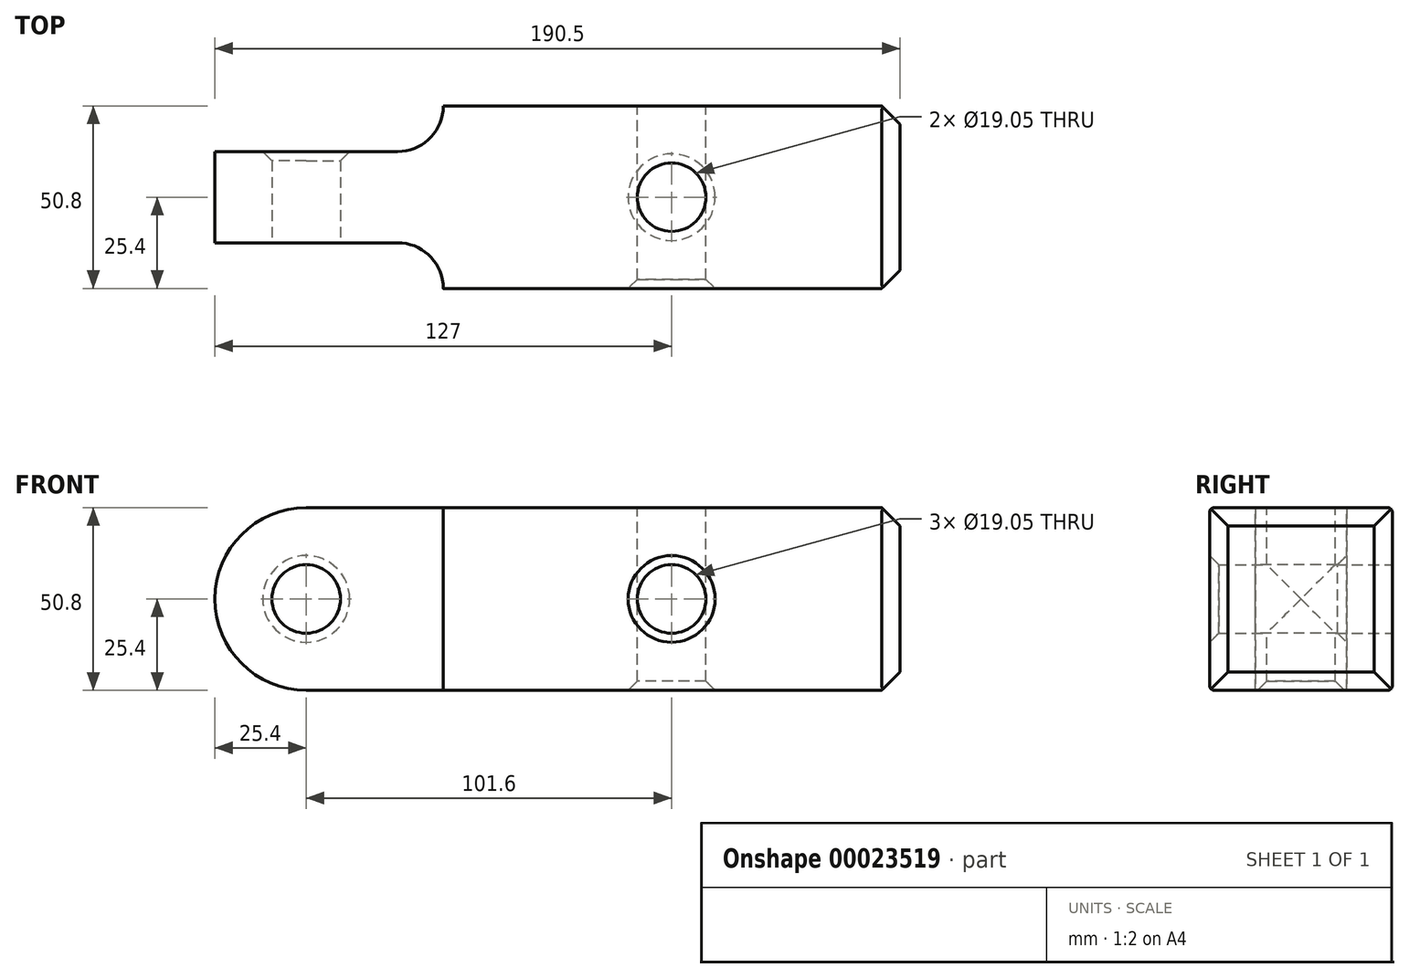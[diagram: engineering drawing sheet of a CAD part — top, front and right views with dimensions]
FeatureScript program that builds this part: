
annotation { "Feature Type Name" : "Feature", "Feature Type Description" : "" }
export const myFeature = defineFeature(function(context is Context, id is Id, definition is map)
    precondition{}
    {
        {
            var Q0;
            Q0=qCreatedBy(makeId("Right.planeOp"),FACE);
            var sketch = newSketch(context, id + "F0", { "sketchPlane" : qUnion([Q0])});
            skLineSegment(sketch, "E0.bottom", {"start": v(0, 0) * mm, "end": v(50.8, 0) * mm});
            skLineSegment(sketch, "E0.top", {"start": v(0, 50.8) * mm, "end": v(50.8, 50.8) * mm});
            skLineSegment(sketch, "E0.left", {"start": v(0, 0) * mm, "end": v(0, 50.8) * mm});
            skLineSegment(sketch, "E0.right", {"start": v(50.8, 0) * mm, "end": v(50.8, 50.8) * mm});
            skSolve(sketch);
        }
        {
            var Q0;
            Q0 = qSketchRegion(id + "F0", true);
            extrude(context, id + "F1", {"entities" : qUnion([Q0]), "depth" : 190.5 * mm});
        }
        {
            var Q0;
            Q0=makeQuery(id+"F1.opExtrude","CAP_FACE",FACE,{"disambiguationData":[OSD([sQuery(id+"F0.wireOp",EDGE,"E0.bottom"),sQuery(id+"F0.wireOp",EDGE,"E0.top"),sQuery(id+"F0.wireOp",EDGE,"E0.left"),sQuery(id+"F0.wireOp",EDGE,"E0.right")])],"isStart":false});
            chamfer(context, id + "F2", {"entities" : qUnion([Q0]), "width" : 5.08 * mm, "tangentPropagation" : true});
        }
        {
            var Q0;
            Q0=makeQuery(id+"F1.opExtrude","SWEPT_FACE",FACE,{"disambiguationData":[OSD([sQuery(id+"F0.wireOp",EDGE,"E0.right")])]});
            var sketch = newSketch(context, id + "F3", { "sketchPlane" : qUnion([Q0])});
            skCircle(sketch, "E1", {"center": v(-127, 25.4) * mm, "radius": 9.53 * mm});
            skLineSegment(sketch, "E2", {"start": v(0, 25.4) * mm, "end": v(-185.42, 25.4) * mm, "construction": true});
            skSolve(sketch);
        }
        {
            var Q0;
            Q0 = qSketchRegion(id + "F3", true);
            extrude(context, id + "F4", {"entities" : qUnion([Q0]), "operationType" : NewBodyOperationType.REMOVE, "endBound" : BoundingType.THROUGH_ALL, "oppositeDirection" : true, "depth" : 25.4 * mm});
        }
        {
            var Q0;
            Q0=makeQuery(id+"F1.opExtrude","SWEPT_EDGE",EDGE,{"disambiguationData":[OSD([sQuery(id+"F0.wireOp",EDGE,"E0.top"),sQuery(id+"F0.wireOp",EDGE,"E0.right")])]});
            var Q1;
            Q1=makeQuery(id+"F1.opExtrude","SWEPT_EDGE",EDGE,{"disambiguationData":[OSD([sQuery(id+"F0.wireOp",EDGE,"E0.top"),sQuery(id+"F0.wireOp",EDGE,"E0.left")])]});
            var Q2;
            Q2=makeQuery(id+"F1.opExtrude","SWEPT_EDGE",EDGE,{"disambiguationData":[OSD([sQuery(id+"F0.wireOp",EDGE,"E0.bottom"),sQuery(id+"F0.wireOp",EDGE,"E0.right")])]});
            var Q3;
            Q3=makeQuery(id+"F1.opExtrude","SWEPT_EDGE",EDGE,{"disambiguationData":[OSD([sQuery(id+"F0.wireOp",EDGE,"E0.bottom"),sQuery(id+"F0.wireOp",EDGE,"E0.left")])]});
            fillet(context, id + "F5", {"entities" : qUnion([Q0, Q1, Q2, Q3]), "radius" : 1.27 * mm, "tangentPropagation" : true, "allowEdgeOverflow" : false});
        }
        {
            var Q0;
            Q0=makeQuery(id+"F4.boolean.opBoolean","COPY",EDGE,{"derivedFrom":makeQuery(id+"F4.opExtrude","CAP_EDGE",EDGE,{"disambiguationData":[OSD([sQuery(id+"F3.wireOp",EDGE,"E1")])],"isStart":true})});
            var Q1;
            Q1=makeQuery(id+"F4.boolean.opBoolean","INTERSECT",EDGE,{"derivedFrom":[makeQuery(id+"F1.opExtrude","SWEPT_FACE",FACE,{"disambiguationData":[OSD([sQuery(id+"F0.wireOp",EDGE,"E0.left")])]}),makeQuery(id+"F4.opExtrude","SWEPT_FACE",FACE,{"disambiguationData":[OSD([sQuery(id+"F3.wireOp",EDGE,"E1")])]})]});
            chamfer(context, id + "F6", {"entities" : qUnion([Q0, Q1]), "width" : 2.54 * mm});
        }
        {
            var Q0;
            Q0=makeQuery(id+"F1.opExtrude","CAP_FACE",FACE,{"disambiguationData":[OSD([sQuery(id+"F0.wireOp",EDGE,"E0.bottom"),sQuery(id+"F0.wireOp",EDGE,"E0.top"),sQuery(id+"F0.wireOp",EDGE,"E0.left"),sQuery(id+"F0.wireOp",EDGE,"E0.right")])],"isStart":true});
            var sketch = newSketch(context, id + "F7", { "sketchPlane" : qUnion([Q0])});
            skLineSegment(sketch, "E3", {"start": v(-25.4, 50.8) * mm, "end": v(-25.4, 0) * mm, "construction": true});
            skLineSegment(sketch, "E4.bottom", {"start": v(-97.35, 92.06) * mm, "end": v(-38.1, 92.06) * mm});
            skLineSegment(sketch, "E4.top", {"start": v(-97.35, -26.43) * mm, "end": v(-38.1, -26.43) * mm});
            skLineSegment(sketch, "E4.left", {"start": v(-97.35, 92.06) * mm, "end": v(-97.35, -26.43) * mm});
            skLineSegment(sketch, "E4.right", {"start": v(-38.1, 92.06) * mm, "end": v(-38.1, -26.43) * mm});
            skLineSegment(sketch, "E5.bottom", {"start": v(-12.7, 97.83) * mm, "end": v(35.91, 97.83) * mm});
            skLineSegment(sketch, "E5.top", {"start": v(-12.7, -31.6) * mm, "end": v(35.91, -31.6) * mm});
            skLineSegment(sketch, "E5.left", {"start": v(-12.7, 97.83) * mm, "end": v(-12.7, -31.6) * mm});
            skLineSegment(sketch, "E5.right", {"start": v(35.91, 97.83) * mm, "end": v(35.91, -31.6) * mm});
            skSolve(sketch);
        }
        {
            var Q0;
            Q0 = qSketchRegion(id + "F7", true);
            extrude(context, id + "F8", {"entities" : qUnion([Q0]), "operationType" : NewBodyOperationType.REMOVE, "oppositeDirection" : true, "depth" : 63.5 * mm});
        }
        {
            var Q0;
            Q0=makeQuery(id+"F1.opExtrude","CAP_EDGE",EDGE,{"disambiguationData":[OSD([sQuery(id+"F0.wireOp",EDGE,"E0.top")])],"isStart":true});
            var Q1;
            Q1=makeQuery(id+"F1.opExtrude","CAP_EDGE",EDGE,{"disambiguationData":[OSD([sQuery(id+"F0.wireOp",EDGE,"E0.bottom")])],"isStart":true});
            fillet(context, id + "F9", {"entities" : qUnion([Q0, Q1]), "radius" : 25.4 * mm, "tangentPropagation" : true, "allowEdgeOverflow" : false});
        }
        {
            var Q0;
            Q0=makeQuery(id+"F8.boolean.opBoolean","COPY",FACE,{"derivedFrom":makeQuery(id+"F8.opExtrude","SWEPT_FACE",FACE,{"disambiguationData":[OSD([sQuery(id+"F7.wireOp",EDGE,"E5.left")])]})});
            var sketch = newSketch(context, id + "F10", { "sketchPlane" : qUnion([Q0])});
            skCircle(sketch, "E6", {"center": v(25.4, 25.4) * mm, "radius": 9.53 * mm});
            skSolve(sketch);
        }
        {
            var Q0;
            Q0 = qSketchRegion(id + "F10", true);
            extrude(context, id + "F11", {"entities" : qUnion([Q0]), "operationType" : NewBodyOperationType.REMOVE, "oppositeDirection" : true, "depth" : 77.11 * mm});
        }
        {
            var Q0;
            Q0=makeQuery(id+"F11.boolean.opBoolean","COPY",EDGE,{"derivedFrom":makeQuery(id+"F11.opExtrude","CAP_EDGE",EDGE,{"disambiguationData":[OSD([sQuery(id+"F10.wireOp",EDGE,"E6")])],"isStart":true})});
            var Q1;
            Q1=makeQuery(id+"F11.boolean.opBoolean","INTERSECT",EDGE,{"derivedFrom":[makeQuery(id+"F8.boolean.opBoolean","COPY",FACE,{"derivedFrom":makeQuery(id+"F8.opExtrude","SWEPT_FACE",FACE,{"disambiguationData":[OSD([sQuery(id+"F7.wireOp",EDGE,"E4.right")])]})}),makeQuery(id+"F11.opExtrude","SWEPT_FACE",FACE,{"disambiguationData":[OSD([sQuery(id+"F10.wireOp",EDGE,"E6")])]})]});
            chamfer(context, id + "F12", {"entities" : qUnion([Q0, Q1]), "width" : 2.54 * mm, "tangentPropagation" : true});
        }
        {
            var Q0;
            Q0=makeQuery(id+"F8.boolean.opBoolean","COPY",EDGE,{"derivedFrom":makeQuery(id+"F8.opExtrude","CAP_EDGE",EDGE,{"disambiguationData":[OSD([sQuery(id+"F7.wireOp",EDGE,"E5.left")])],"isStart":false})});
            var Q1;
            Q1=makeQuery(id+"F8.boolean.opBoolean","COPY",EDGE,{"derivedFrom":makeQuery(id+"F8.opExtrude","CAP_EDGE",EDGE,{"disambiguationData":[OSD([sQuery(id+"F7.wireOp",EDGE,"E4.right")])],"isStart":false})});
            fillet(context, id + "F13", {"entities" : qUnion([Q0, Q1]), "radius" : 12.7 * mm, "tangentPropagation" : true, "allowEdgeOverflow" : false});
        }
        {
            var Q0;
            Q0=makeQuery(id+"F1.opExtrude","SWEPT_FACE",FACE,{"disambiguationData":[OSD([sQuery(id+"F0.wireOp",EDGE,"E0.top")])]});
            var sketch = newSketch(context, id + "F14", { "sketchPlane" : qUnion([Q0])});
            skLineSegment(sketch, "E7", {"start": v(185.42, 25.4) * mm, "end": v(127, 25.4) * mm, "construction": true});
            skCircle(sketch, "E8", {"center": v(127, 25.4) * mm, "radius": 9.53 * mm});
            skSolve(sketch);
        }
        {
            var Q0;
            Q0 = qSketchRegion(id + "F14", true);
            extrude(context, id + "F15", {"entities" : qUnion([Q0]), "operationType" : NewBodyOperationType.REMOVE, "endBound" : BoundingType.THROUGH_ALL, "oppositeDirection" : true, "depth" : 25.4 * mm});
        }
        {
            var Q0;
            Q0=makeQuery(id+"F15.boolean.opBoolean","COPY",EDGE,{"derivedFrom":makeQuery(id+"F15.opExtrude","CAP_EDGE",EDGE,{"disambiguationData":[OSD([sQuery(id+"F14.wireOp",EDGE,"E8")])],"isStart":true})});
            var Q1;
            Q1=makeQuery(id+"F15.boolean.opBoolean","INTERSECT",EDGE,{"derivedFrom":[makeQuery(id+"F1.opExtrude","SWEPT_FACE",FACE,{"disambiguationData":[OSD([sQuery(id+"F0.wireOp",EDGE,"E0.bottom")])]}),makeQuery(id+"F15.opExtrude","SWEPT_FACE",FACE,{"disambiguationData":[OSD([sQuery(id+"F14.wireOp",EDGE,"E8")])]})]});
            chamfer(context, id + "F16", {"entities" : qUnion([Q0, Q1]), "width" : 2.54 * mm, "tangentPropagation" : true});
        }
    });
